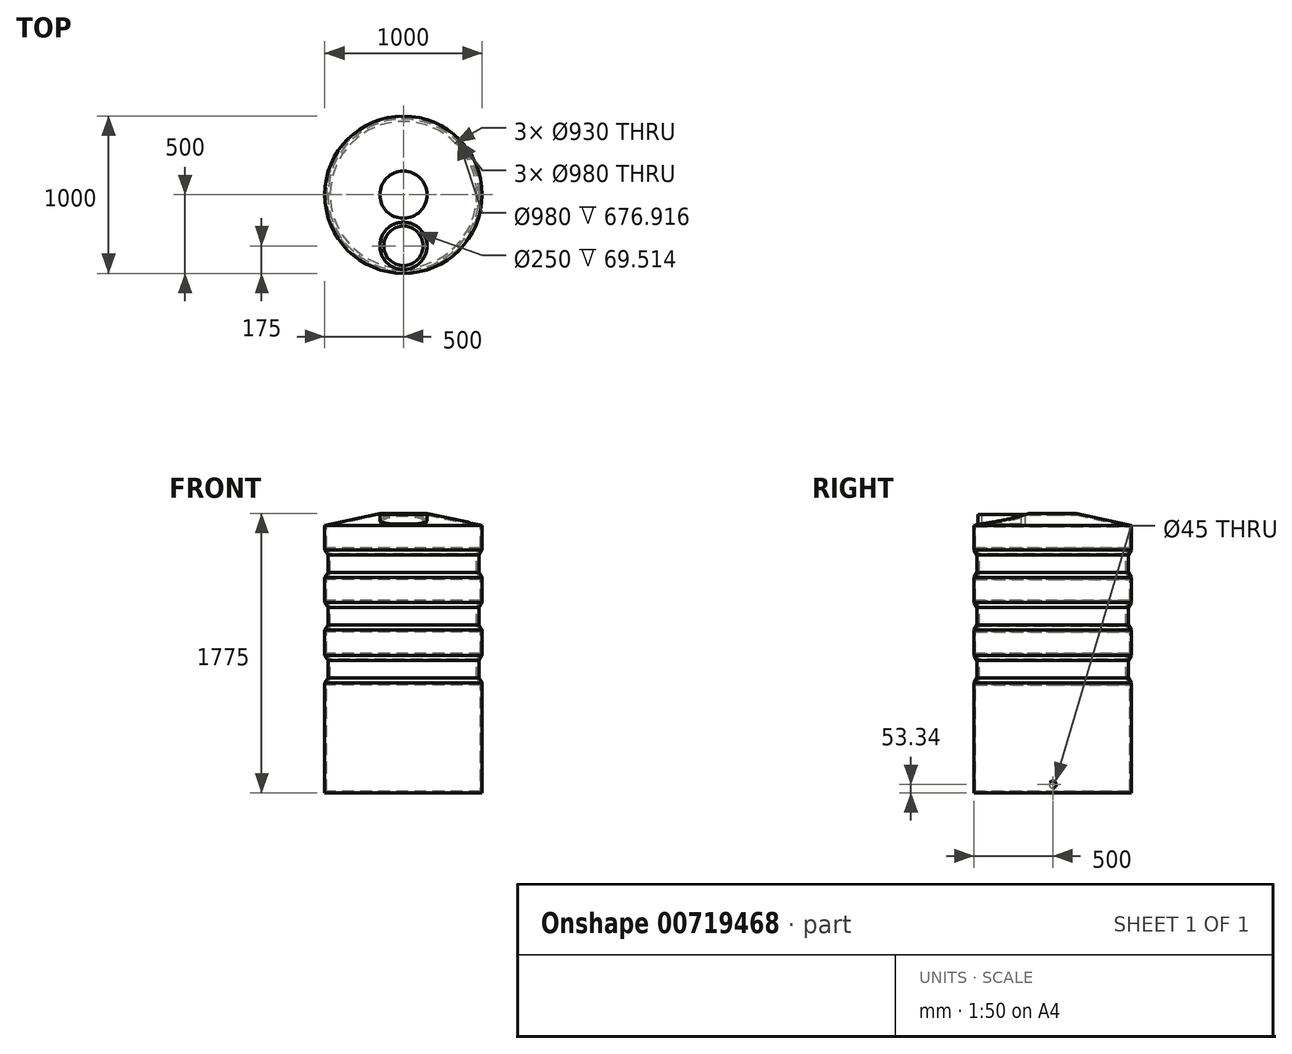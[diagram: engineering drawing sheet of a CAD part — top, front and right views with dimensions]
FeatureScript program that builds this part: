
annotation { "Feature Type Name" : "Feature", "Feature Type Description" : "" }
export const myFeature = defineFeature(function(context is Context, id is Id, definition is map)
    precondition{}
    {
        {
            var Q0;
            Q0=qCreatedBy(makeId("Front.planeOp"),FACE);
            var sketch = newSketch(context, id + "F0", { "sketchPlane" : qUnion([Q0])});
            skLineSegment(sketch, "E0", {"start": v(0, -753.34) * mm, "end": v(-500, -753.34) * mm});
            skLineSegment(sketch, "E1", {"start": v(-500, -753.34) * mm, "end": v(-500, -54.12) * mm});
            skLineSegment(sketch, "E2", {"start": v(-500, 946.66) * mm, "end": v(-150, 1021.66) * mm});
            skLineSegment(sketch, "E3", {"start": v(-150, 1021.66) * mm, "end": v(0, 1021.66) * mm});
            skLineSegment(sketch, "E4.0", {"start": v(-148.94, 1011.66) * mm, "end": v(0, 1011.66) * mm});
            skLineSegment(sketch, "E4.1", {"start": v(-490, 938.58) * mm, "end": v(-148.94, 1011.66) * mm});
            skLineSegment(sketch, "E4.2", {"start": v(-490, -743.34) * mm, "end": v(-490, -66.42) * mm});
            skLineSegment(sketch, "E4.3", {"start": v(0, -743.34) * mm, "end": v(-490, -743.34) * mm});
            skLineSegment(sketch, "E5", {"start": v(0, 1021.66) * mm, "end": v(0, -743.34) * mm, "construction": true});
            skLineSegment(sketch, "E6", {"start": v(0, -753.34) * mm, "end": v(0, -743.34) * mm});
            skLineSegment(sketch, "E7", {"start": v(0, 1021.66) * mm, "end": v(0, 1011.66) * mm});
            skLineSegment(sketch, "E8", {"start": v(-490, 803.58) * mm, "end": v(-465, 763.58) * mm});
            skLineSegment(sketch, "E9", {"start": v(-465, 763.58) * mm, "end": v(-465, 643.58) * mm});
            skLineSegment(sketch, "E10", {"start": v(-465, 643.58) * mm, "end": v(-490, 603.58) * mm});
            skLineSegment(sketch, "E11", {"start": v(-490, 468.58) * mm, "end": v(-465, 428.58) * mm});
            skLineSegment(sketch, "E12", {"start": v(-465, 428.58) * mm, "end": v(-465, 308.58) * mm});
            skLineSegment(sketch, "E13", {"start": v(-465, 308.58) * mm, "end": v(-490, 268.58) * mm});
            skLineSegment(sketch, "E14", {"start": v(-490, 133.58) * mm, "end": v(-465, 93.58) * mm});
            skLineSegment(sketch, "E15", {"start": v(-465, 93.58) * mm, "end": v(-465, -26.42) * mm});
            skLineSegment(sketch, "E16", {"start": v(-465, -26.42) * mm, "end": v(-490, -66.42) * mm});
            skLineSegment(sketch, "E17.trimOffspring", {"start": v(-490, 133.58) * mm, "end": v(-490, 268.58) * mm});
            skLineSegment(sketch, "E18.trimOffspring", {"start": v(-490, 468.58) * mm, "end": v(-490, 603.58) * mm});
            skLineSegment(sketch, "E19.trimOffspring", {"start": v(-490, 803.58) * mm, "end": v(-490, 938.58) * mm});
            skLineSegment(sketch, "E20.0", {"start": v(-480, 647.88) * mm, "end": v(-500, 615.88) * mm});
            skLineSegment(sketch, "E20.1", {"start": v(-480, 759.28) * mm, "end": v(-480, 647.88) * mm});
            skLineSegment(sketch, "E20.2", {"start": v(-500, 791.28) * mm, "end": v(-480, 759.28) * mm});
            skLineSegment(sketch, "E21.trimOffspring", {"start": v(-500, 791.28) * mm, "end": v(-500, 946.66) * mm});
            skLineSegment(sketch, "E22.0", {"start": v(-480, 312.88) * mm, "end": v(-500, 280.88) * mm});
            skLineSegment(sketch, "E22.1", {"start": v(-480, 424.28) * mm, "end": v(-480, 312.88) * mm});
            skLineSegment(sketch, "E22.2", {"start": v(-500, 456.28) * mm, "end": v(-480, 424.28) * mm});
            skLineSegment(sketch, "E23.trimOffspring", {"start": v(-500, 456.28) * mm, "end": v(-500, 615.88) * mm});
            skLineSegment(sketch, "E24.0", {"start": v(-480, -22.12) * mm, "end": v(-500, -54.12) * mm});
            skLineSegment(sketch, "E24.1", {"start": v(-480, 89.28) * mm, "end": v(-480, -22.12) * mm});
            skLineSegment(sketch, "E24.2", {"start": v(-500, 121.28) * mm, "end": v(-480, 89.28) * mm});
            skLineSegment(sketch, "E25.trimOffspring", {"start": v(-500, 121.28) * mm, "end": v(-500, 280.88) * mm});
            skSolve(sketch);
        }
        {
            var Q0;
            Q0 = qSketchRegion(id + "F0", true);
            var Q1;
            Q1=sQuery(id+"F0.wireOp",EDGE,"E5");
            revolve(context, id + "F1", {"surfaceOperationType" : NewSurfaceOperationType.NEW, "entities" : qUnion([Q0]), "axis" : qUnion([Q1]), "revolveType" : RevolveType.FULL});
        }
        {
            var Q0;
            Q0=makeQuery(id+"F1.opRevolve","SWEPT_FACE",FACE,{"disambiguationData":[OSD([sQuery(id+"F0.wireOp",EDGE,"E3")])]});
            var sketch = newSketch(context, id + "F2", { "sketchPlane" : qUnion([Q0])});
            skLineSegment(sketch, "E26", {"start": v(0, 0) * mm, "end": v(0, -500) * mm, "construction": true});
            skPoint(sketch, "E27", {"position": v(0, -150) * mm});
            skPoint(sketch, "E28", {"position": v(0, -325) * mm});
            skCircle(sketch, "E29", {"center": v(0, -325) * mm, "radius": 150 * mm});
            skCircle(sketch, "E30", {"center": v(0, -325) * mm, "radius": 125 * mm});
            skSolve(sketch);
        }
        {
            var Q0;
            Q0=sQuery(id+"F2.wireOp",VERTEX,"E28");
            var Q1;
            Q1=makeQuery(id+"F1.opRevolve","SWEPT_BODY",BODY,{"disambiguationData":[OSD([sQuery(id+"F0.wireOp",EDGE,"E0"),sQuery(id+"F0.wireOp",EDGE,"E1"),sQuery(id+"F0.wireOp",EDGE,"E2"),sQuery(id+"F0.wireOp",EDGE,"E3"),sQuery(id+"F0.wireOp",EDGE,"E4.0"),sQuery(id+"F0.wireOp",EDGE,"E4.1"),sQuery(id+"F0.wireOp",EDGE,"E4.2"),sQuery(id+"F0.wireOp",EDGE,"E4.3"),sQuery(id+"F0.wireOp",EDGE,"E6"),sQuery(id+"F0.wireOp",EDGE,"E7")])]});
            hole(context, id + "F3", {"style" : HoleStyle.SIMPLE, "endStyle" : HoleEndStyle.BLIND, "holeDiameter" : 250 * mm, "majorDiameter" : 5 * mm, "holeDepth" : 1000 * mm, "isTappedThrough" : true, "tappedDepth" : 12 * mm, "tapClearance" : 3, "startFromSketch" : true, "locations" : qUnion([Q0]), "scope" : qUnion([Q1])});
        }
        {
            var Q0;
            Q0=qCreatedBy(makeId("Right.planeOp"),FACE);
            var sketch = newSketch(context, id + "F4", { "sketchPlane" : qUnion([Q0])});
            skLineSegment(sketch, "E31", {"start": v(0, 0) * mm, "end": v(0, -700) * mm, "construction": true});
            skSolve(sketch);
        }
        {
            var Q0;
            Q0=sQuery(id+"F4.wireOp",VERTEX,"E31.end");
            var Q1;
            Q1=makeQuery(id+"F1.opRevolve","SWEPT_BODY",BODY,{"disambiguationData":[OSD([sQuery(id+"F0.wireOp",EDGE,"E0"),sQuery(id+"F0.wireOp",EDGE,"E1"),sQuery(id+"F0.wireOp",EDGE,"E2"),sQuery(id+"F0.wireOp",EDGE,"E3"),sQuery(id+"F0.wireOp",EDGE,"E4.0"),sQuery(id+"F0.wireOp",EDGE,"E4.1"),sQuery(id+"F0.wireOp",EDGE,"E4.2"),sQuery(id+"F0.wireOp",EDGE,"E4.3"),sQuery(id+"F0.wireOp",EDGE,"E6"),sQuery(id+"F0.wireOp",EDGE,"E7")])]});
            hole(context, id + "F5", {"style" : HoleStyle.SIMPLE, "endStyle" : HoleEndStyle.BLIND, "oppositeDirection" : true, "holeDiameter" : 45 * mm, "majorDiameter" : 5 * mm, "holeDepth" : 600 * mm, "isTappedThrough" : true, "tappedDepth" : 12 * mm, "tapClearance" : 3, "startFromSketch" : true, "locations" : qUnion([Q0]), "scope" : qUnion([Q1])});
        }
        {
            var Q0;
            Q0=makeQuery(id+"F2.imprint","IMPRINT",FACE,{"disambiguationData":[TD([[makeQuery(id+"F2.imprint","IMPRINT",EDGE,{"derivedFrom":sQuery(id+"F2.wireOp",EDGE,"E29")}),1.0]])]});
            extrude(context, id + "F6", {"entities" : qUnion([Q0]), "operationType" : NewBodyOperationType.ADD, "oppositeDirection" : true, "depth" : 67.5 * mm, "offsetDistance" : 25 * mm, "hasSecondDirection" : true, "secondDirectionOppositeDirection" : true, "secondDirectionDepth" : 5 * mm});
        }
    });
